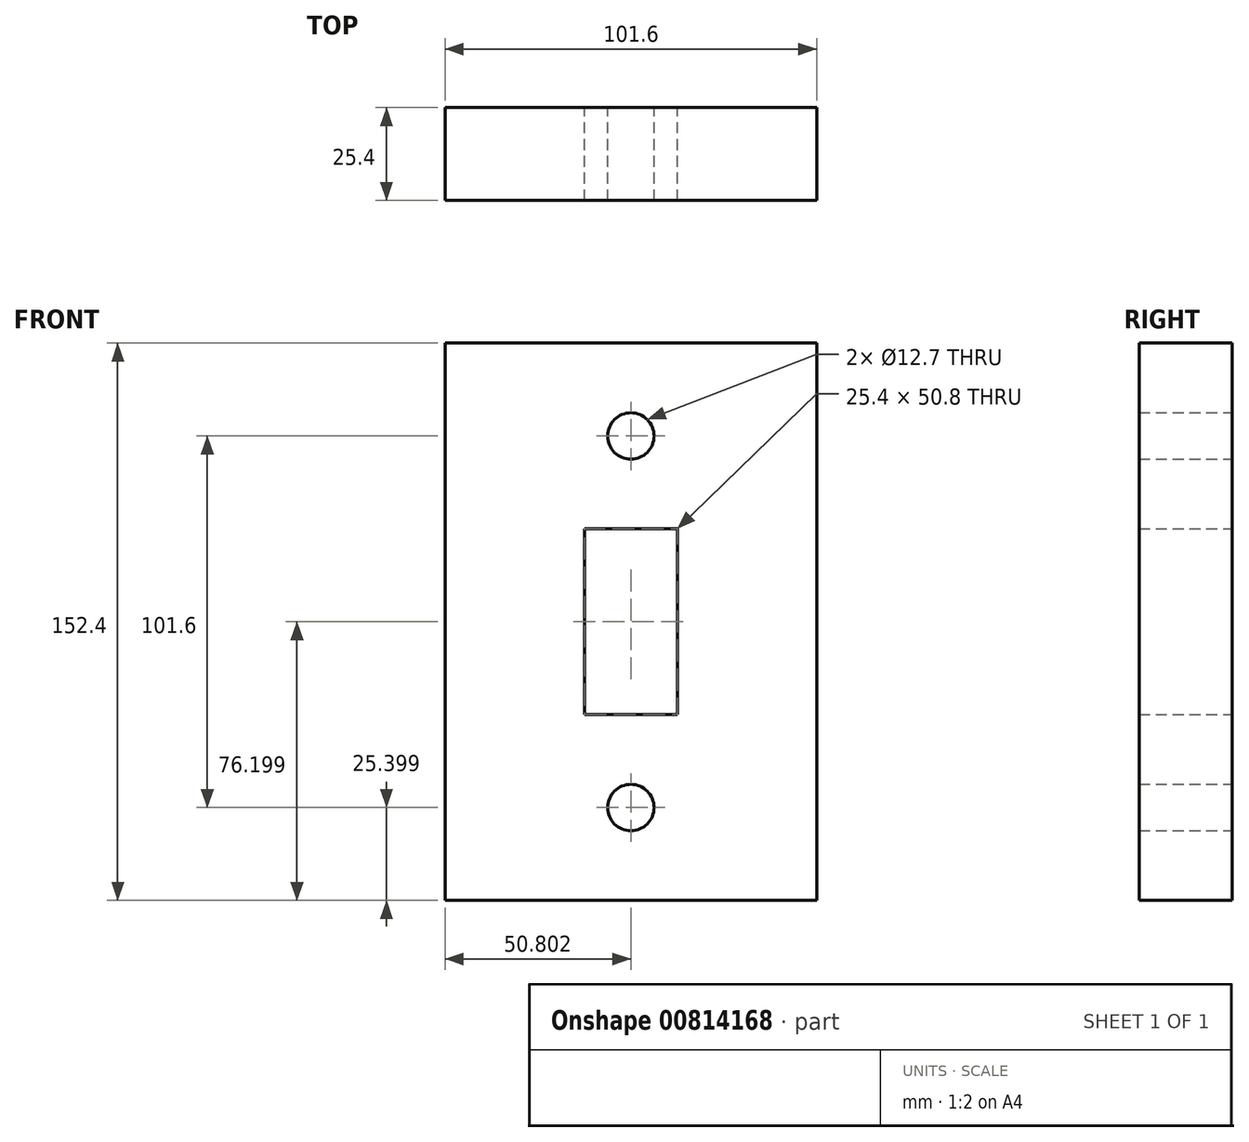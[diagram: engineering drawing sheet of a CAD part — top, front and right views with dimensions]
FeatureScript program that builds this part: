
annotation { "Feature Type Name" : "Feature", "Feature Type Description" : "" }
export const myFeature = defineFeature(function(context is Context, id is Id, definition is map)
    precondition{}
    {
        {
            var Q0;
            Q0=qCreatedBy(makeId("Front.planeOp"),FACE);
            var sketch = newSketch(context, id + "F0", { "sketchPlane" : qUnion([Q0])});
            skLineSegment(sketch, "E0.bottom", {"start": v(-104.46, -44.7) * mm, "end": v(-2.86, -44.7) * mm});
            skLineSegment(sketch, "E0.top", {"start": v(-104.46, 107.7) * mm, "end": v(-2.86, 107.7) * mm});
            skLineSegment(sketch, "E0.left", {"start": v(-104.46, -44.7) * mm, "end": v(-104.46, 107.7) * mm});
            skLineSegment(sketch, "E0.right", {"start": v(-2.86, -44.7) * mm, "end": v(-2.86, 107.7) * mm});
            skLineSegment(sketch, "E1.bottom", {"start": v(-66.36, 6.1) * mm, "end": v(-40.96, 6.1) * mm});
            skLineSegment(sketch, "E1.top", {"start": v(-66.36, 56.9) * mm, "end": v(-40.96, 56.9) * mm});
            skLineSegment(sketch, "E1.left", {"start": v(-66.36, 6.1) * mm, "end": v(-66.36, 56.9) * mm});
            skLineSegment(sketch, "E1.right", {"start": v(-40.96, 6.1) * mm, "end": v(-40.96, 56.9) * mm});
            skCircle(sketch, "E2", {"center": v(-53.66, 82.3) * mm, "radius": 6.35 * mm});
            skCircle(sketch, "E3", {"center": v(-53.66, -19.3) * mm, "radius": 6.35 * mm});
            skPoint(sketch, "E3.centerSnap0", {"position": v(-53.66, 6.1) * mm});
            skSolve(sketch);
        }
        {
            var Q0;
            Q0 = qSketchRegion(id + "F0", true);
            extrude(context, id + "F1", {"entities" : qUnion([Q0]), "depth" : 25.4 * mm, "offsetDistance" : 25.4 * mm});
        }
    });
